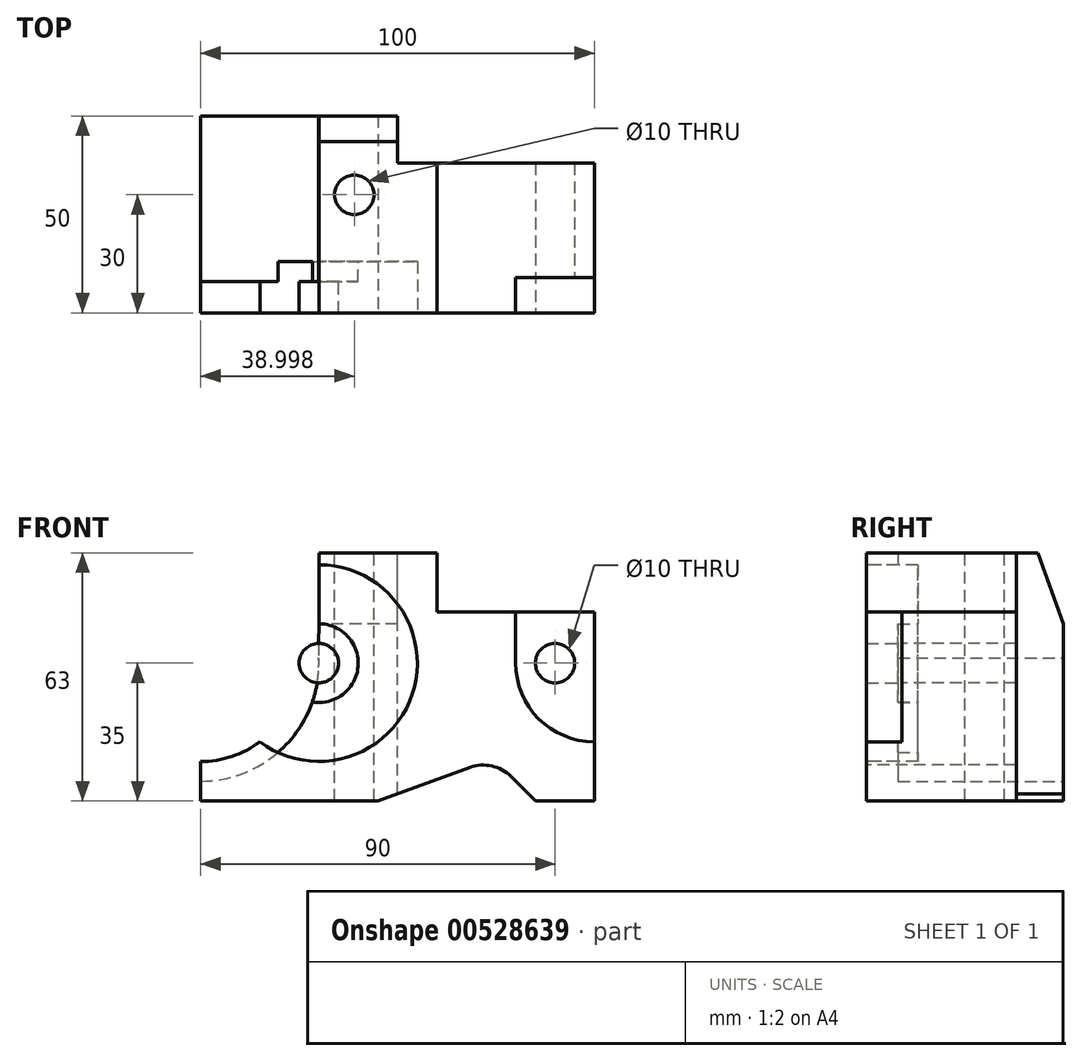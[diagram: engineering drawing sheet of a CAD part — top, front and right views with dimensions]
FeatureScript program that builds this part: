
annotation { "Feature Type Name" : "Feature", "Feature Type Description" : "" }
export const myFeature = defineFeature(function(context is Context, id is Id, definition is map)
    precondition{}
    {
        {
            var Q0;
            Q0=qCreatedBy(makeId("Front.planeOp"),FACE);
            var sketch = newSketch(context, id + "F0", { "sketchPlane" : qUnion([Q0])});
            skLineSegment(sketch, "E0.bottom", {"start": v(-50, 31.5) * mm, "end": v(50, 31.5) * mm});
            skLineSegment(sketch, "E0.top", {"start": v(-50, -31.5) * mm, "end": v(-5, -31.5) * mm});
            skLineSegment(sketch, "E0.left", {"start": v(-50, 31.5) * mm, "end": v(-50, -31.5) * mm});
            skLineSegment(sketch, "E0.right", {"start": v(50, 31.5) * mm, "end": v(50, -31.5) * mm});
            skLineSegment(sketch, "E1", {"start": v(-50, -31.5) * mm, "end": v(50, 31.5) * mm, "construction": true});
            skLineSegment(sketch, "E2", {"start": v(-5, -31.5) * mm, "end": v(18.34, -23) * mm});
            skLineSegment(sketch, "E3", {"start": v(35, -31.5) * mm, "end": v(28.83, -25.33) * mm});
            skLineSegment(sketch, "E4.trimOffspring", {"start": v(35, -31.5) * mm, "end": v(50, -31.5) * mm});
            skPoint(sketch, "E5.visualSharp", {"position": v(24.33, -20.83) * mm});
            skArc(sketch, "E5.filletArc", {"start": v(28.83, -25.33) * mm, "mid": v(23.92, -22.64) * mm, "end": v(18.34, -23) * mm});
            skSolve(sketch);
        }
        {
            var Q0;
            Q0 = qSketchRegion(id + "F0", true);
            extrude(context, id + "F1", {"entities" : qUnion([Q0]), "oppositeDirection" : true, "depth" : 50 * mm, "offsetDistance" : 25 * mm});
        }
        {
            var Q0;
            Q0=makeQuery(id+"F1.opExtrude","CAP_FACE",FACE,{"disambiguationData":[OSD([sQuery(id+"F0.wireOp",EDGE,"E0.bottom"),sQuery(id+"F0.wireOp",EDGE,"E0.top"),sQuery(id+"F0.wireOp",EDGE,"E0.left"),sQuery(id+"F0.wireOp",EDGE,"E0.right"),sQuery(id+"F0.wireOp",EDGE,"E2"),sQuery(id+"F0.wireOp",EDGE,"E3"),sQuery(id+"F0.wireOp",EDGE,"E4.trimOffspring"),sQuery(id+"F0.wireOp",EDGE,"E5.filletArc")])],"isStart":true});
            var sketch = newSketch(context, id + "F2", { "sketchPlane" : qUnion([Q0])});
            skLineSegment(sketch, "E6", {"start": v(-50, 3.5) * mm, "end": v(-36.63, 3.5) * mm, "construction": true});
            skCircle(sketch, "E7", {"center": v(-50, 3.5) * mm, "radius": 25 * mm});
            skSolve(sketch);
        }
        {
            var Q0;
            Q0 = qSketchRegion(id + "F2", true);
            extrude(context, id + "F3", {"entities" : qUnion([Q0]), "operationType" : NewBodyOperationType.REMOVE, "endBound" : BoundingType.THROUGH_ALL, "oppositeDirection" : true, "depth" : 25 * mm, "offsetDistance" : 25 * mm});
        }
        {
            var Q0;
            Q0=makeQuery(id+"F1.opExtrude","CAP_FACE",FACE,{"disambiguationData":[OSD([sQuery(id+"F0.wireOp",EDGE,"E0.bottom"),sQuery(id+"F0.wireOp",EDGE,"E0.top"),sQuery(id+"F0.wireOp",EDGE,"E0.left"),sQuery(id+"F0.wireOp",EDGE,"E0.right"),sQuery(id+"F0.wireOp",EDGE,"E2"),sQuery(id+"F0.wireOp",EDGE,"E3"),sQuery(id+"F0.wireOp",EDGE,"E4.trimOffspring"),sQuery(id+"F0.wireOp",EDGE,"E5.filletArc")])],"isStart":true});
            var sketch = newSketch(context, id + "F4", { "sketchPlane" : qUnion([Q0])});
            skPoint(sketch, "E8.endSnap0", {"position": v(50, 0) * mm});
            skPoint(sketch, "E9.endSnap0", {"position": v(-50, -26.5) * mm});
            skLineSegment(sketch, "E10", {"start": v(-20, -31.5) * mm, "end": v(-20, 3.5) * mm, "construction": true});
            skPoint(sketch, "E11.orphan", {"position": v(-46.24, 0) * mm});
            skCircle(sketch, "E12", {"center": v(-20, 3.5) * mm, "radius": 25 * mm});
            skSolve(sketch);
        }
        {
            var Q0;
            Q0 = qSketchRegion(id + "F4", true);
            extrude(context, id + "F5", {"entities" : qUnion([Q0]), "operationType" : NewBodyOperationType.REMOVE, "oppositeDirection" : true, "depth" : 13 * mm, "offsetDistance" : 25 * mm});
        }
        {
            var Q0;
            Q0=makeQuery(id+"F5.boolean.opBoolean","COPY",FACE,{"derivedFrom":makeQuery(id+"F5.opExtrude","CAP_FACE",FACE,{"disambiguationData":[OSD([sQuery(id+"F4.wireOp",EDGE,"E12")])],"isStart":false})});
            var sketch = newSketch(context, id + "F6", { "sketchPlane" : qUnion([Q0])});
            skCircle(sketch, "E13", {"center": v(-20, 3.5) * mm, "radius": 10 * mm});
            skSolve(sketch);
        }
        {
            var Q0;
            Q0 = qSketchRegion(id + "F6", true);
            extrude(context, id + "F7", {"entities" : qUnion([Q0]), "operationType" : NewBodyOperationType.ADD, "depth" : 5 * mm, "offsetDistance" : 25 * mm});
        }
        {
            var Q0;
            Q0=makeQuery(id+"F7.opExtrude","CAP_FACE",FACE,{"disambiguationData":[OSD([sQuery(id+"F6.wireOp",EDGE,"E13")])],"isStart":false});
            var sketch = newSketch(context, id + "F8", { "sketchPlane" : qUnion([Q0])});
            skCircle(sketch, "E14", {"center": v(-20, 3.5) * mm, "radius": 5 * mm});
            skSolve(sketch);
        }
        {
            var Q0;
            Q0 = qSketchRegion(id + "F8", true);
            extrude(context, id + "F9", {"entities" : qUnion([Q0]), "operationType" : NewBodyOperationType.ADD, "depth" : 8 * mm, "offsetDistance" : 25 * mm});
        }
        {
            var Q0;
            Q0=makeQuery(id+"F1.opExtrude","CAP_FACE",FACE,{"disambiguationData":[OSD([sQuery(id+"F0.wireOp",EDGE,"E0.bottom"),sQuery(id+"F0.wireOp",EDGE,"E0.top"),sQuery(id+"F0.wireOp",EDGE,"E0.left"),sQuery(id+"F0.wireOp",EDGE,"E0.right"),sQuery(id+"F0.wireOp",EDGE,"E2"),sQuery(id+"F0.wireOp",EDGE,"E3"),sQuery(id+"F0.wireOp",EDGE,"E4.trimOffspring"),sQuery(id+"F0.wireOp",EDGE,"E5.filletArc")])],"isStart":false});
            var sketch = newSketch(context, id + "F10", { "sketchPlane" : qUnion([Q0])});
            skArc(sketch, "E15", {"start": v(20.03, 4.85) * mm, "mid": v(70.69, -18.22) * mm, "end": v(50.1, 33.5) * mm});
            skLineSegment(sketch, "E16", {"start": v(50, -31.5) * mm, "end": v(50, 3.5) * mm, "construction": true});
            skLineSegment(sketch, "E17", {"start": v(20, 13.5) * mm, "end": v(20, 33.5) * mm});
            skLineSegment(sketch, "E18", {"start": v(50.1, 33.5) * mm, "end": v(20, 33.5) * mm});
            skLineSegment(sketch, "E19", {"start": v(20, 13.5) * mm, "end": v(20.03, 4.85) * mm});
            skSolve(sketch);
        }
        {
            var Q0;
            Q0 = qSketchRegion(id + "F10", true);
            extrude(context, id + "F11", {"entities" : qUnion([Q0]), "operationType" : NewBodyOperationType.REMOVE, "oppositeDirection" : true, "depth" : 42 * mm, "offsetDistance" : 25 * mm});
        }
        {
            var Q0;
            {var subQ0=sQuery(id+"F10.wireOp",EDGE,"mzNQvssG-Mvp5-FWXz-dt48-1w95TP1N98JV");Q0=makeQuery(id+"F11.boolean.opBoolean","COPY",FACE,{"disambiguationData":[TD([makeQuery(id+"F1.opExtrude","SWEPT_FACE",FACE,{"disambiguationData":[OSD([sQuery(id+"F0.wireOp",EDGE,"E0.bottom")])]}),makeQuery(id+"F1.opExtrude","SWEPT_FACE",FACE,{"disambiguationData":[OSD([sQuery(id+"F0.wireOp",EDGE,"E0.left")])]}),makeQuery(id+"F3.boolean.opBoolean","COPY",FACE,{"derivedFrom":makeQuery(id+"F3.opExtrude","SWEPT_FACE",FACE,{"disambiguationData":[OSD([sQuery(id+"F2.wireOp",EDGE,"E7")])]})}),makeQuery(id+"F5.boolean.opBoolean","COPY",FACE,{"derivedFrom":makeQuery(id+"F5.opExtrude","SWEPT_FACE",FACE,{"disambiguationData":[OSD([sQuery(id+"F4.wireOp",EDGE,"E12")])]})}),makeQuery(id+"F11.opExtrude","SWEPT_FACE",FACE,{"disambiguationData":[OSD([subQ0])]})])],"derivedFrom":makeQuery(id+"F11.opExtrude","CAP_FACE",FACE,{"disambiguationData":[OSD([sQuery(id+"F10.wireOp",EDGE,"E15"),subQ0,sQuery(id+"F10.wireOp",EDGE,"E18"),sQuery(id+"F10.wireOp",EDGE,"E19")])],"isStart":false})});}
            var sketch = newSketch(context, id + "F12", { "sketchPlane" : qUnion([Q0])});
            skLineSegment(sketch, "E20", {"start": v(20, 31.5) * mm, "end": v(20.04, 13.4) * mm});
            skLineSegment(sketch, "E21", {"start": v(20.04, 13.4) * mm, "end": v(50, 13.4) * mm});
            skLineSegment(sketch, "E22", {"start": v(50, 31.5) * mm, "end": v(20, 31.5) * mm});
            skLineSegment(sketch, "E23", {"start": v(50, 31.5) * mm, "end": v(50, 13.4) * mm});
            skSolve(sketch);
        }
        {
            var Q0;
            Q0 = qSketchRegion(id + "F12", true);
            extrude(context, id + "F13", {"entities" : qUnion([Q0]), "operationType" : NewBodyOperationType.REMOVE, "endBound" : BoundingType.THROUGH_ALL, "oppositeDirection" : true, "depth" : 25 * mm, "offsetDistance" : 25 * mm});
        }
        {
            var Q0;
            Q0=makeQuery(id+"F1.opExtrude","CAP_FACE",FACE,{"disambiguationData":[OSD([sQuery(id+"F0.wireOp",EDGE,"E0.bottom"),sQuery(id+"F0.wireOp",EDGE,"E0.top"),sQuery(id+"F0.wireOp",EDGE,"E0.left"),sQuery(id+"F0.wireOp",EDGE,"E0.right"),sQuery(id+"F0.wireOp",EDGE,"E2"),sQuery(id+"F0.wireOp",EDGE,"E3"),sQuery(id+"F0.wireOp",EDGE,"E4.trimOffspring"),sQuery(id+"F0.wireOp",EDGE,"E5.filletArc")])],"isStart":true});
            var sketch = newSketch(context, id + "F14", { "sketchPlane" : qUnion([Q0])});
            skLineSegment(sketch, "E24", {"start": v(10, 31.5) * mm, "end": v(10, 16.5) * mm});
            skLineSegment(sketch, "E25", {"start": v(10, 16.5) * mm, "end": v(50, 16.5) * mm});
            skLineSegment(sketch, "E26", {"start": v(10, 31.5) * mm, "end": v(50, 31.5) * mm});
            skLineSegment(sketch, "E27", {"start": v(50, 31.5) * mm, "end": v(50, 16.5) * mm});
            skSolve(sketch);
        }
        {
            var Q0;
            Q0 = qSketchRegion(id + "F14", true);
            extrude(context, id + "F15", {"entities" : qUnion([Q0]), "operationType" : NewBodyOperationType.REMOVE, "endBound" : BoundingType.THROUGH_ALL, "oppositeDirection" : true, "depth" : 25 * mm, "offsetDistance" : 25 * mm});
        }
        {
            var Q0;
            Q0=makeQuery(id+"F1.opExtrude","CAP_FACE",FACE,{"disambiguationData":[OSD([sQuery(id+"F0.wireOp",EDGE,"E0.bottom"),sQuery(id+"F0.wireOp",EDGE,"E0.top"),sQuery(id+"F0.wireOp",EDGE,"E0.left"),sQuery(id+"F0.wireOp",EDGE,"E0.right"),sQuery(id+"F0.wireOp",EDGE,"E2"),sQuery(id+"F0.wireOp",EDGE,"E3"),sQuery(id+"F0.wireOp",EDGE,"E4.trimOffspring"),sQuery(id+"F0.wireOp",EDGE,"E5.filletArc")])],"isStart":true});
            var sketch = newSketch(context, id + "F16", { "sketchPlane" : qUnion([Q0])});
            skLineSegment(sketch, "E28", {"start": v(30, 3.5) * mm, "end": v(30, 16.5) * mm});
            skLineSegment(sketch, "E29", {"start": v(30, 16.5) * mm, "end": v(50, 16.5) * mm});
            skArc(sketch, "E30", {"start": v(30, 3.5) * mm, "mid": v(35.86, -10.64) * mm, "end": v(50, -16.5) * mm});
            skLineSegment(sketch, "E31", {"start": v(50, 16.5) * mm, "end": v(50, -16.5) * mm});
            skSolve(sketch);
        }
        {
            var Q0;
            Q0 = qSketchRegion(id + "F16", true);
            extrude(context, id + "F17", {"entities" : qUnion([Q0]), "operationType" : NewBodyOperationType.REMOVE, "oppositeDirection" : true, "depth" : 9 * mm, "offsetDistance" : 25 * mm});
        }
        {
            var Q0;
            Q0=makeQuery(id+"F17.boolean.opBoolean","COPY",FACE,{"derivedFrom":makeQuery(id+"F17.opExtrude","CAP_FACE",FACE,{"disambiguationData":[OSD([sQuery(id+"F16.wireOp",EDGE,"E28"),sQuery(id+"F16.wireOp",EDGE,"E29"),sQuery(id+"F16.wireOp",EDGE,"E30"),sQuery(id+"F16.wireOp",EDGE,"E31")])],"isStart":false})});
            var sketch = newSketch(context, id + "F18", { "sketchPlane" : qUnion([Q0])});
            skCircle(sketch, "E32", {"center": v(40, 3.5) * mm, "radius": 5 * mm});
            skSolve(sketch);
        }
        {
            var Q0;
            Q0 = qSketchRegion(id + "F18", true);
            extrude(context, id + "F19", {"entities" : qUnion([Q0]), "operationType" : NewBodyOperationType.REMOVE, "endBound" : BoundingType.THROUGH_ALL, "oppositeDirection" : true, "depth" : 25 * mm, "offsetDistance" : 25 * mm});
        }
        {
            var Q0;
            Q0=makeQuery(id+"F1.opExtrude","SWEPT_FACE",FACE,{"disambiguationData":[OSD([sQuery(id+"F0.wireOp",EDGE,"E0.bottom")])]});
            var sketch = newSketch(context, id + "F20", { "sketchPlane" : qUnion([Q0])});
            skLineSegment(sketch, "E33", {"start": v(0, 50) * mm, "end": v(0, 38) * mm});
            skLineSegment(sketch, "E34", {"start": v(0, 38) * mm, "end": v(50, 38) * mm});
            skLineSegment(sketch, "E35", {"start": v(50, 38) * mm, "end": v(50, 50) * mm});
            skLineSegment(sketch, "E36", {"start": v(50, 50) * mm, "end": v(0, 50) * mm});
            skSolve(sketch);
        }
        {
            var Q0;
            Q0 = qSketchRegion(id + "F20", true);
            extrude(context, id + "F21", {"entities" : qUnion([Q0]), "operationType" : NewBodyOperationType.REMOVE, "endBound" : BoundingType.THROUGH_ALL, "oppositeDirection" : true, "depth" : 25 * mm, "offsetDistance" : 25 * mm});
        }
        {
            var Q0;
            Q0=makeQuery(id+"F11.boolean.opBoolean","COPY",FACE,{"derivedFrom":makeQuery(id+"F11.opExtrude","SWEPT_FACE",FACE,{"disambiguationData":[OSD([sQuery(id+"F10.wireOp",EDGE,"E17")])]})});
            var sketch = newSketch(context, id + "F22", { "sketchPlane" : qUnion([Q0])});
            skLineSegment(sketch, "E37", {"start": v(-50, 31.5) * mm, "end": v(-50, 13.5) * mm});
            skLineSegment(sketch, "E38", {"start": v(-50, 13.5) * mm, "end": v(-43.45, 31.5) * mm});
            skLineSegment(sketch, "E39", {"start": v(-43.45, 31.5) * mm, "end": v(-50, 31.5) * mm});
            skSolve(sketch);
        }
        {
            var Q0;
            Q0 = qSketchRegion(id + "F22", true);
            extrude(context, id + "F23", {"entities" : qUnion([Q0]), "operationType" : NewBodyOperationType.REMOVE, "endBound" : BoundingType.THROUGH_ALL, "oppositeDirection" : true, "depth" : 25 * mm, "offsetDistance" : 25 * mm});
        }
        {
            var Q0;
            Q0=makeQuery(id+"F1.opExtrude","SWEPT_FACE",FACE,{"disambiguationData":[OSD([sQuery(id+"F0.wireOp",EDGE,"E0.bottom")])]});
            var sketch = newSketch(context, id + "F24", { "sketchPlane" : qUnion([Q0])});
            skCircle(sketch, "E40", {"center": v(-11, 30) * mm, "radius": 5 * mm});
            skSolve(sketch);
        }
        {
            var Q0;
            Q0 = qSketchRegion(id + "F24", true);
            extrude(context, id + "F25", {"entities" : qUnion([Q0]), "operationType" : NewBodyOperationType.REMOVE, "endBound" : BoundingType.THROUGH_ALL, "oppositeDirection" : true, "depth" : 25 * mm, "offsetDistance" : 25 * mm});
        }
    });
